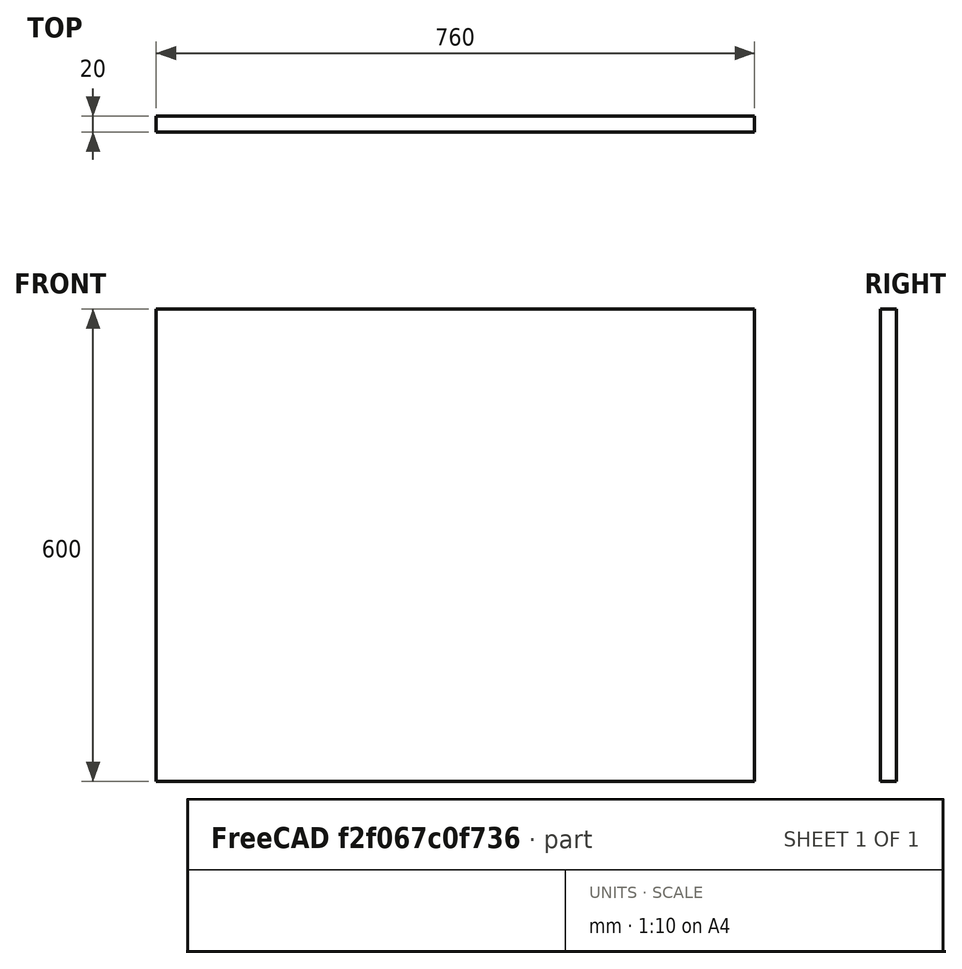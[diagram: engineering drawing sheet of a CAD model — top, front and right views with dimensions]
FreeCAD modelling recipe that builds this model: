
FCSTD DOCUMENT  (FreeCAD 0.20R29603 (Git))
Label: Rückenlehne
License: All rights reserved
LicenseURL: http://en.wikipedia.org/wiki/All_rights_reserved
objects: Sketcher::SketchObject×1, PartDesign::Pad×1, PartDesign::Body×1
note: 4 computed .brp shape members not serialized (recipe doc carries the construction recipe); baked Part::Feature solids carry a one-line shape summary decoded from their .brp

FEATURE [Sketcher::SketchObject] Sketch
  FullyConstrained = true
  MapMode = 5
  Placement = pos=(0,0,0) rot=(1,0,0;1.5708rad)
  Support = -> [XZ_Plane]
  sketch-geometry (5):
    g0: LineSegment StartX=-380 StartY=300 StartZ=0 EndX=-380 EndY=-300 EndZ=0
    g1: LineSegment StartX=-380 StartY=-300 StartZ=0 EndX=380 EndY=-300 EndZ=0
    g2: LineSegment StartX=380 StartY=-300 StartZ=0 EndX=380 EndY=300 EndZ=0
    g3: LineSegment StartX=380 StartY=300 StartZ=0 EndX=-380 EndY=300 EndZ=0
    g4: GeomPoint X=0 Y=0 Z=0
  constraints (12):
    c: Coincident(g0,g1)
    c: Coincident(g1,g2)
    c: Coincident(g2,g3)
    c: Coincident(g3,g0)
    c: Horizontal(g1)
    c: Horizontal(g3)
    c: Vertical(g0)
    c: Vertical(g2)
    c: Symmetric(g1,g0,g4)
    c: Coincident(g4,g-1)
    c: Distance(g3) = 760
    c: Distance(g0) = 600
FEATURE [PartDesign::Pad] Pad
  Direction = (0,-1,2e-16)
  Length = 20
  Length2 = 10
  Placement = pos=(0,0,0) rot=(1,0,0;1.5708rad)
  Profile = -> Sketch
  ReferenceAxis = -> Sketch [N_Axis]
  Type = 0
FEATURE [PartDesign::Body] Body
  Group = -> [Sketch,Pad]
  Origin = -> Origin
  Tip = -> Pad
